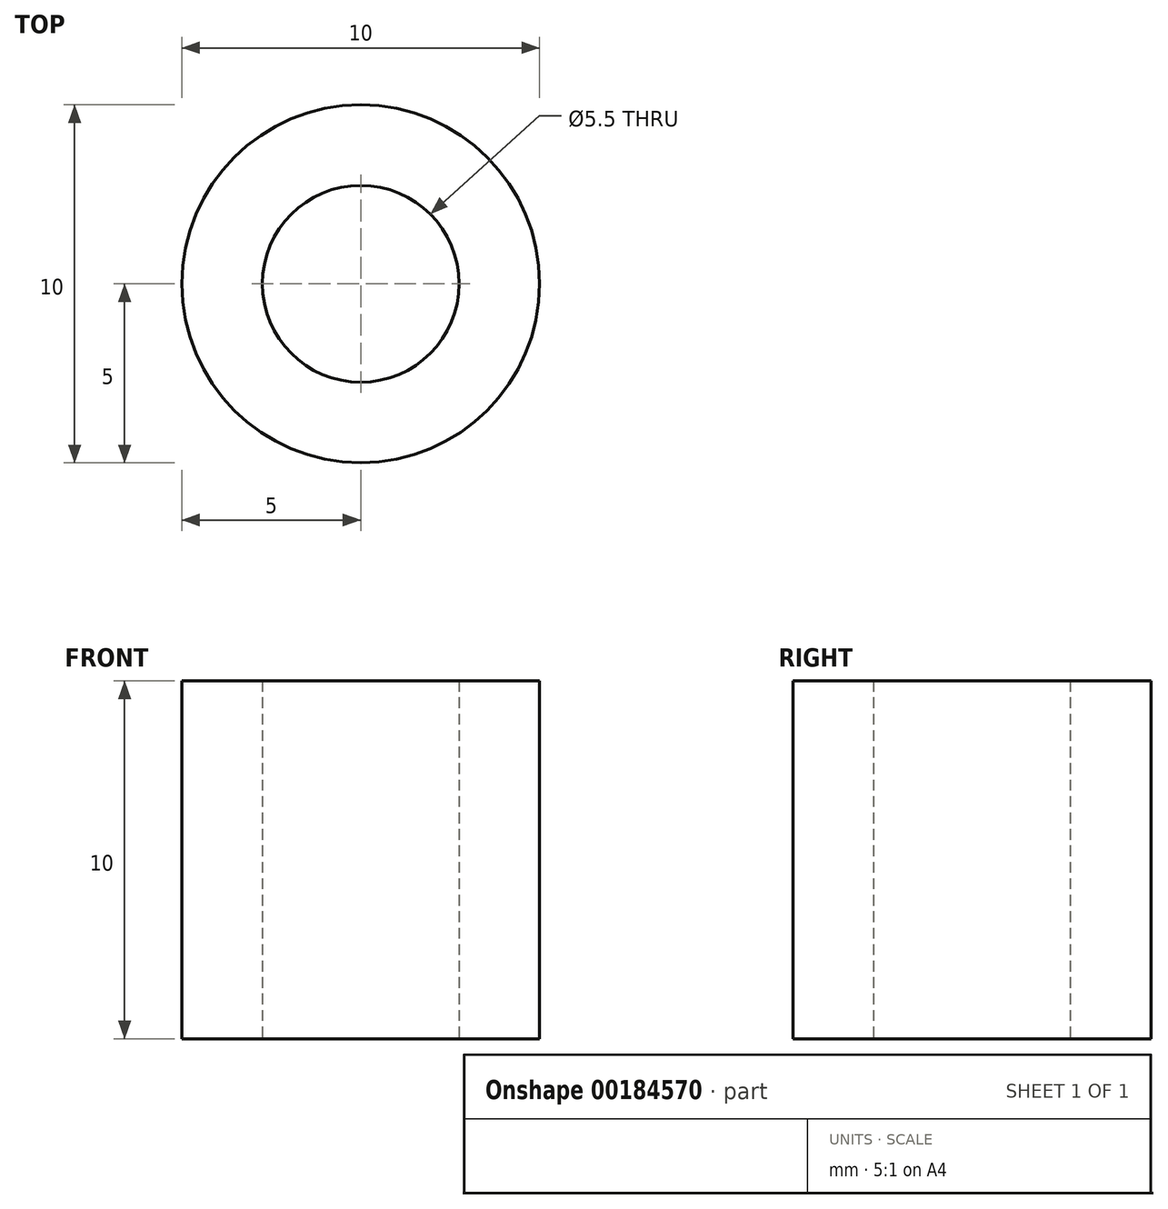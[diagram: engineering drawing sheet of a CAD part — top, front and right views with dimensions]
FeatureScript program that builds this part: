
annotation { "Feature Type Name" : "Feature", "Feature Type Description" : "" }
export const myFeature = defineFeature(function(context is Context, id is Id, definition is map)
    precondition{}
    {
        {
            var Q0;
            Q0=qCreatedBy(makeId("Top.planeOp"),FACE);
            var sketch = newSketch(context, id + "F0", { "sketchPlane" : qUnion([Q0])});
            skCircle(sketch, "E0", {"center": v(0, 0) * mm, "radius": 5 * mm});
            skCircle(sketch, "E1", {"center": v(0, 0) * mm, "radius": 2.75 * mm});
            skSolve(sketch);
        }
        {
            var Q0;
            Q0=qSketchRegion(id+"F0",true);
            var Q1;
            Q1=makeQuery(id+"F0.imprint","IMPRINT",FACE,{"disambiguationData":[TD([[makeQuery(id+"F0.imprint","IMPRINT",EDGE,{"derivedFrom":sQuery(id+"F0.wireOp",EDGE,"E0")}),1.0]])]});
            extrude(context, id + "F1", {"entities" : qUnion([Q0, Q1]), "depth" : 10 * mm});
        }
    });
